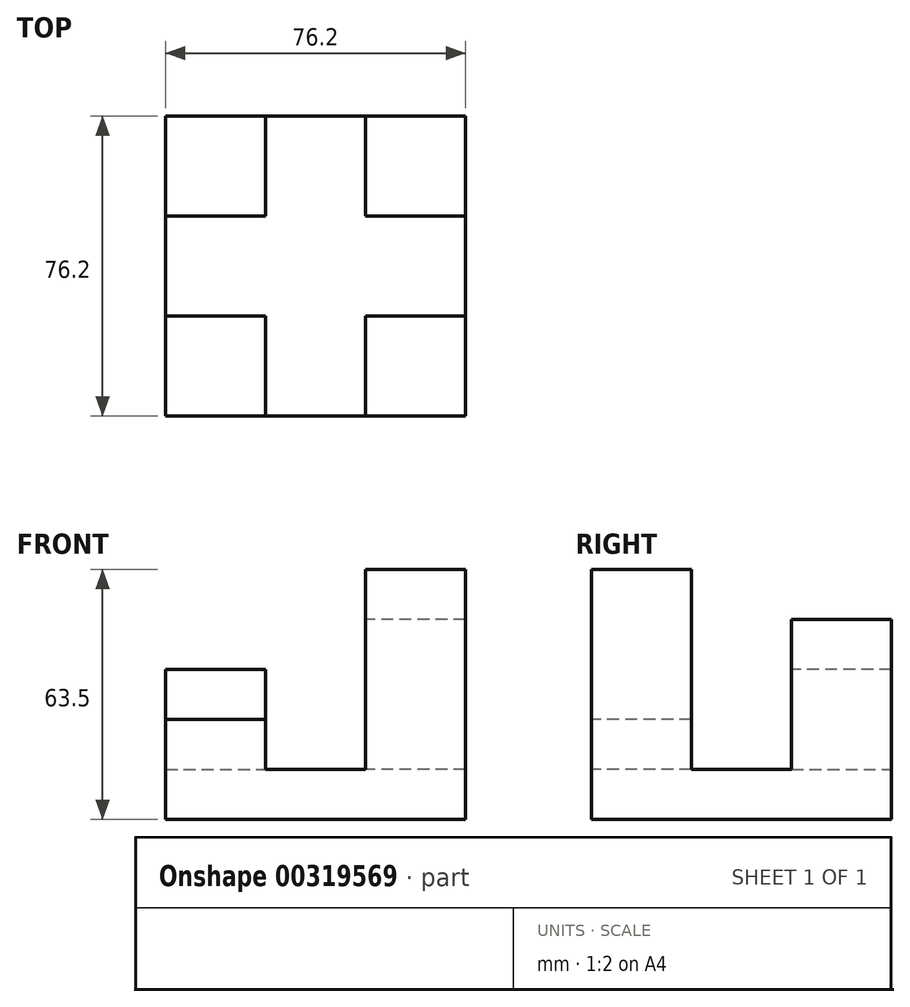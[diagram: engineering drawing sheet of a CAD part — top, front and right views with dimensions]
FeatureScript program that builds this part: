
annotation { "Feature Type Name" : "Feature", "Feature Type Description" : "" }
export const myFeature = defineFeature(function(context is Context, id is Id, definition is map)
    precondition{}
    {
        {
            var Q0;
            Q0=qCreatedBy(makeId("Top.planeOp"),FACE);
            var sketch = newSketch(context, id + "F0", { "sketchPlane" : qUnion([Q0])});
            skLineSegment(sketch, "E0", {"start": v(-42.74, 41.34) * mm, "end": v(-42.74, -34.86) * mm});
            skLineSegment(sketch, "E1", {"start": v(-42.74, -34.86) * mm, "end": v(33.46, -34.86) * mm});
            skLineSegment(sketch, "E2", {"start": v(33.46, -34.86) * mm, "end": v(33.46, 41.34) * mm});
            skLineSegment(sketch, "E3", {"start": v(33.46, 41.34) * mm, "end": v(-42.74, 41.34) * mm});
            skSolve(sketch);
        }
        {
            var Q0;
            Q0=makeQuery(id+"F0.imprint","IMPRINT",FACE,{"disambiguationData":[TD([[makeQuery(id+"F0.imprint","IMPRINT",EDGE,{"derivedFrom":sQuery(id+"F0.wireOp",EDGE,"E0")}),1.0]])]});
            extrude(context, id + "F1", {"entities" : qUnion([Q0]), "depth" : 12.7 * mm});
        }
        {
            var Q0;
            Q0=makeQuery(id+"F1.opExtrude","CAP_FACE",FACE,{"disambiguationData":[OSD([sQuery(id+"F0.wireOp",EDGE,"E0"),sQuery(id+"F0.wireOp",EDGE,"E1"),sQuery(id+"F0.wireOp",EDGE,"E2"),sQuery(id+"F0.wireOp",EDGE,"E3")])],"isStart":false});
            var sketch = newSketch(context, id + "F2", { "sketchPlane" : qUnion([Q0])});
            skLineSegment(sketch, "E4", {"start": v(-42.74, 41.34) * mm, "end": v(-42.74, 15.94) * mm});
            skLineSegment(sketch, "E5", {"start": v(-42.74, 15.94) * mm, "end": v(-17.34, 15.94) * mm});
            skLineSegment(sketch, "E6", {"start": v(-17.34, 15.94) * mm, "end": v(-17.34, 41.34) * mm});
            skLineSegment(sketch, "E7", {"start": v(-17.34, 41.34) * mm, "end": v(-42.74, 41.34) * mm});
            skSolve(sketch);
        }
        {
            var Q0;
            Q0=makeQuery(id+"F2.imprint","IMPRINT",FACE,{"disambiguationData":[TD([[makeQuery(id+"F2.imprint","IMPRINT",EDGE,{"derivedFrom":sQuery(id+"F2.wireOp",EDGE,"E4")}),1.0]])]});
            extrude(context, id + "F3", {"entities" : qUnion([Q0]), "operationType" : NewBodyOperationType.ADD, "depth" : 25.4 * mm});
        }
        {
            var Q0;
            Q0=makeQuery(id+"F1.opExtrude","CAP_FACE",FACE,{"disambiguationData":[OSD([sQuery(id+"F0.wireOp",EDGE,"E0"),sQuery(id+"F0.wireOp",EDGE,"E1"),sQuery(id+"F0.wireOp",EDGE,"E2"),sQuery(id+"F0.wireOp",EDGE,"E3")])],"isStart":false});
            var sketch = newSketch(context, id + "F4", { "sketchPlane" : qUnion([Q0])});
            skLineSegment(sketch, "E8", {"start": v(33.46, 41.34) * mm, "end": v(33.46, 15.94) * mm});
            skLineSegment(sketch, "E9", {"start": v(33.46, 15.94) * mm, "end": v(8.06, 15.94) * mm});
            skLineSegment(sketch, "E10", {"start": v(8.06, 15.94) * mm, "end": v(8.06, 41.34) * mm});
            skLineSegment(sketch, "E11", {"start": v(8.06, 41.34) * mm, "end": v(33.46, 41.34) * mm});
            skSolve(sketch);
        }
        {
            var Q0;
            Q0=makeQuery(id+"F4.imprint","IMPRINT",FACE,{"disambiguationData":[TD([[makeQuery(id+"F4.imprint","IMPRINT",EDGE,{"derivedFrom":sQuery(id+"F4.wireOp",EDGE,"E8")}),1.0]])]});
            extrude(context, id + "F5", {"entities" : qUnion([Q0]), "operationType" : NewBodyOperationType.ADD, "depth" : 38.1 * mm});
        }
        {
            var Q0;
            Q0=makeQuery(id+"F1.opExtrude","CAP_FACE",FACE,{"disambiguationData":[OSD([sQuery(id+"F0.wireOp",EDGE,"E0"),sQuery(id+"F0.wireOp",EDGE,"E1"),sQuery(id+"F0.wireOp",EDGE,"E2"),sQuery(id+"F0.wireOp",EDGE,"E3")])],"isStart":false});
            var sketch = newSketch(context, id + "F6", { "sketchPlane" : qUnion([Q0])});
            skLineSegment(sketch, "E12", {"start": v(-42.74, -34.86) * mm, "end": v(-17.34, -34.86) * mm});
            skLineSegment(sketch, "E13", {"start": v(-17.34, -34.86) * mm, "end": v(-17.34, -9.46) * mm});
            skLineSegment(sketch, "E14", {"start": v(-17.34, -9.46) * mm, "end": v(-42.74, -9.46) * mm});
            skLineSegment(sketch, "E15", {"start": v(-42.74, -9.46) * mm, "end": v(-42.74, -34.86) * mm});
            skSolve(sketch);
        }
        {
            var Q0;
            Q0=makeQuery(id+"F6.imprint","IMPRINT",FACE,{"disambiguationData":[TD([[makeQuery(id+"F6.imprint","IMPRINT",EDGE,{"derivedFrom":sQuery(id+"F6.wireOp",EDGE,"E12")}),1.0]])]});
            extrude(context, id + "F7", {"entities" : qUnion([Q0]), "operationType" : NewBodyOperationType.ADD, "depth" : 12.7 * mm});
        }
        {
            var Q0;
            Q0=makeQuery(id+"F1.opExtrude","CAP_FACE",FACE,{"disambiguationData":[OSD([sQuery(id+"F0.wireOp",EDGE,"E0"),sQuery(id+"F0.wireOp",EDGE,"E1"),sQuery(id+"F0.wireOp",EDGE,"E2"),sQuery(id+"F0.wireOp",EDGE,"E3")])],"isStart":false});
            var sketch = newSketch(context, id + "F8", { "sketchPlane" : qUnion([Q0])});
            skLineSegment(sketch, "E16", {"start": v(33.46, -34.86) * mm, "end": v(33.46, -9.46) * mm});
            skLineSegment(sketch, "E17", {"start": v(33.46, -9.46) * mm, "end": v(8.06, -9.46) * mm});
            skLineSegment(sketch, "E18", {"start": v(8.06, -9.46) * mm, "end": v(8.06, -34.86) * mm});
            skLineSegment(sketch, "E19", {"start": v(8.06, -34.86) * mm, "end": v(33.46, -34.86) * mm});
            skSolve(sketch);
        }
        {
            var Q0;
            Q0=makeQuery(id+"F8.imprint","IMPRINT",FACE,{"disambiguationData":[TD([[makeQuery(id+"F8.imprint","IMPRINT",EDGE,{"derivedFrom":sQuery(id+"F8.wireOp",EDGE,"E16")}),1.0]])]});
            extrude(context, id + "F9", {"entities" : qUnion([Q0]), "operationType" : NewBodyOperationType.ADD, "depth" : 50.8 * mm});
        }
    });
